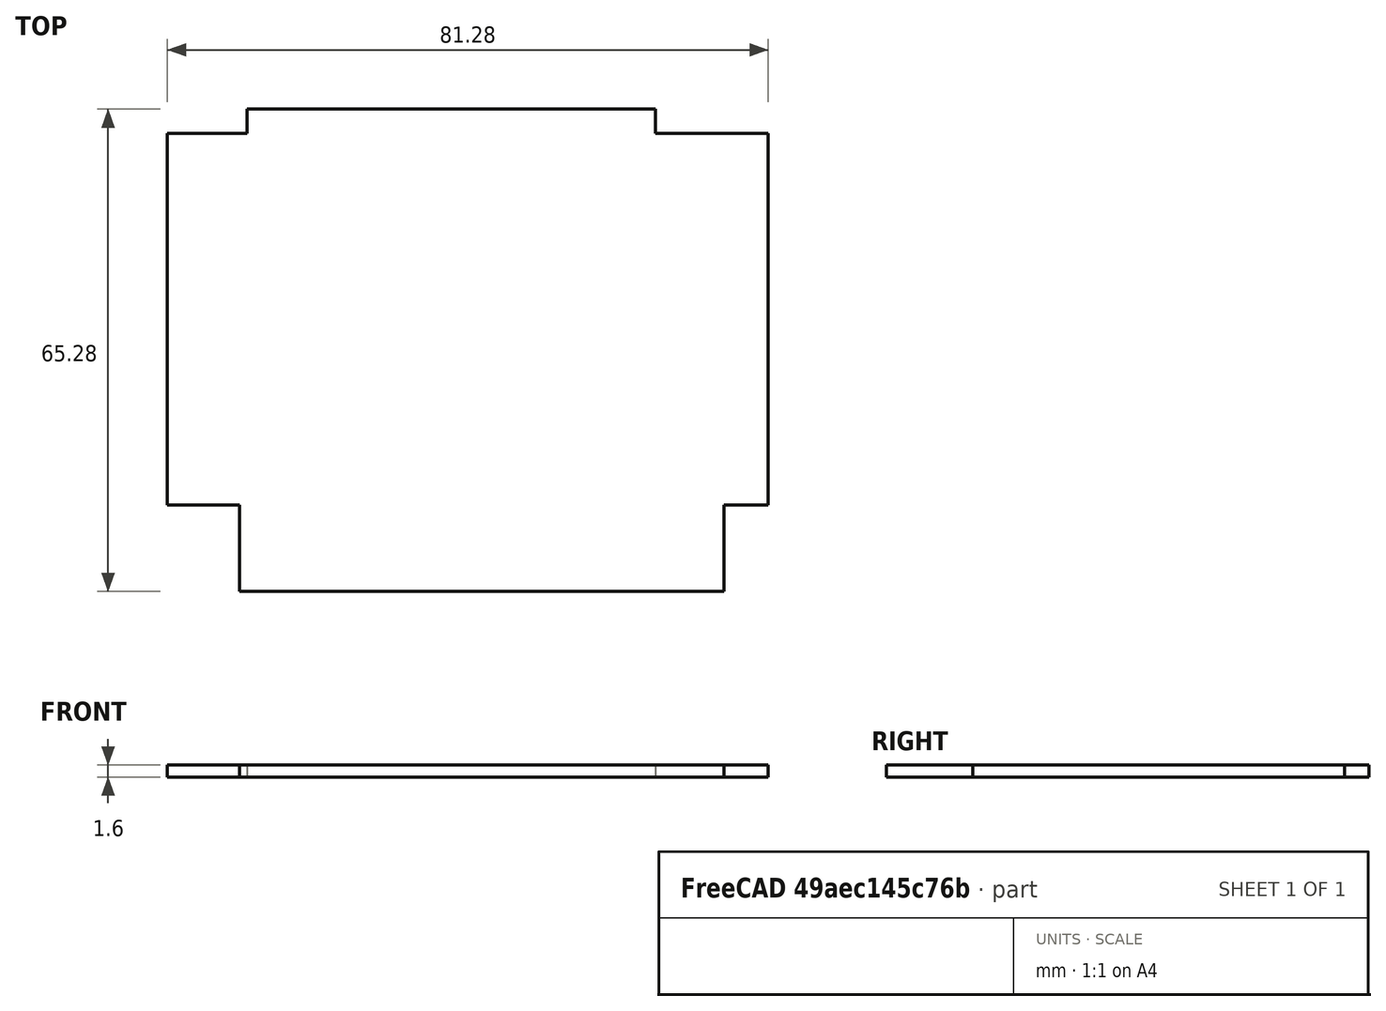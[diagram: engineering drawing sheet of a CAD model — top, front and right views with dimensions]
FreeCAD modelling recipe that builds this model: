
FCSTD DOCUMENT  (FreeCAD 0.19R24291 (Git))
Label: Cart-dummy
License: All rights reserved
LicenseURL: http://en.wikipedia.org/wiki/All_rights_reserved
objects: Part::Feature×3, App::Part×2, PartDesign::CoordinateSystem×1, Sketcher::SketchObject×1
note: 5 computed .brp shape members not serialized (recipe doc carries the construction recipe); baked Part::Feature solids carry a one-line shape summary decoded from their .brp

FEATURE [PartDesign::CoordinateSystem] Local_CS_e656
  AttacherType = Attacher::AttachEngine3D
FEATURE [Part::Feature] Pcb_e656
  Placement = pos=(-111.76,161.036,0) rot=(0,0,1;0rad)
  shape: bbox 81.28 x 65.28 x 1.6 mm, 16 faces (baked)
FEATURE [Sketcher::SketchObject] PCB_Sketch_e656
  FullyConstrained = false
  sketch-geometry (14):
    g0: LineSegment StartX=66.04 StartY=65.278 StartZ=0 EndX=66.04 EndY=61.976 EndZ=0
    g1: LineSegment StartX=10.795 StartY=65.278 StartZ=0 EndX=10.795 EndY=61.976 EndZ=0
    g2: LineSegment StartX=75.311 StartY=11.684 StartZ=0 EndX=81.28 EndY=11.684 EndZ=0
    g3: LineSegment StartX=75.311 StartY=0 StartZ=0 EndX=75.057 EndY=0 EndZ=0
    g4: LineSegment StartX=9.779 StartY=0 StartZ=0 EndX=10.033 EndY=0 EndZ=0
    g5: LineSegment StartX=9.779 StartY=11.684 StartZ=0 EndX=0 EndY=11.684 EndZ=0
    g6: LineSegment StartX=81.28 StartY=61.976 StartZ=0 EndX=81.28 EndY=11.684 EndZ=0
    g7: LineSegment StartX=66.04 StartY=61.976 StartZ=0 EndX=81.28 EndY=61.976 EndZ=0
    g8: LineSegment StartX=10.795 StartY=65.278 StartZ=0 EndX=66.04 EndY=65.278 EndZ=0
    g9: LineSegment StartX=0 StartY=61.976 StartZ=0 EndX=10.795 EndY=61.976 EndZ=0
    g10: LineSegment StartX=0 StartY=11.684 StartZ=0 EndX=0 EndY=61.976 EndZ=0
    g11: LineSegment StartX=9.779 StartY=0 StartZ=0 EndX=9.779 EndY=11.684 EndZ=0
    g12: LineSegment StartX=75.057 StartY=0 StartZ=0 EndX=10.033 EndY=0 EndZ=0
    g13: LineSegment StartX=75.311 StartY=11.684 StartZ=0 EndX=75.311 EndY=0 EndZ=0
  constraints (14):
    c: Coincident(g5,g10)
    c: Coincident(g9,g10)
    c: Coincident(g4,g11)
    c: Coincident(g5,g11)
    c: Coincident(g4,g12)
    c: Coincident(g1,g9)
    c: Coincident(g1,g8)
    c: Coincident(g0,g7)
    c: Coincident(g0,g8)
    c: Coincident(g3,g12)
    c: Coincident(g3,g13)
    c: Coincident(g2,g13)
    c: Coincident(g2,g6)
    c: Coincident(g6,g7)
FEATURE [Part::Feature] pads_area001  label="topPads_e656"
  Placement = pos=(42.65,6.25,0.022) rot=(0,0,1;0rad)
  shape: bbox 62.46 x 11 x 2e-07 mm, 25 faces, 0 solids (baked)
FEATURE [Part::Feature] pads_area002  label="botPads_e656"
  Placement = pos=(42.65,6.25,-1.62) rot=(0,0,1;0rad)
  shape: bbox 62.46 x 11 x 2e-07 mm, 25 faces, 0 solids (baked)
FEATURE [App::Part] Board_Geoms_e656
  Group = -> [Local_CS_e656,Pcb_e656,PCB_Sketch_e656,pads_area001,pads_area002]
  Origin = -> Origin
FEATURE [App::Part] Board_e656  label="rom128k"
  Group = -> [Board_Geoms_e656]
  Origin = -> Origin001
